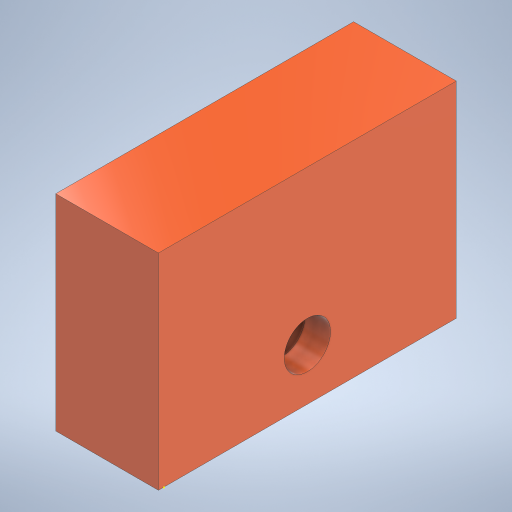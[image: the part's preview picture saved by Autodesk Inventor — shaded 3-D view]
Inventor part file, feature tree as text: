
AUTODESK INVENTOR PART (.ipt)
format: ipt  version: 2024 (Build 280153020, 153B)  size: 206,848 bytes
history: native  units: mm
features: sketch x4, extrude x3
ambient origin geometry x8: Origin, YZ Plane, XZ Plane, XY Plane, X Axis, Y Axis, Z Axis, Center Point
bodies: Solid1 (feature_tree)
feature tree (7):
  extrude  "Extrusion1"  Depth=20.0mm
  sketch  "Sketch6"  dims[d15=2.5mm d16=0.0mm d17=0.5mm]
  extrude  "Extrusion6"  Depth=0.5mm
  extrude  "Extrusion7"  Depth=10.0mm TaperAngle=0.0deg
  sketch  "Sketch1"  dims[d0=20.0mm d1=0.0mm d14=4.5mm]
  sketch  "Sketch7"  dims[d18=0.5mm d19=10.0mm d20=0.0mm]
  sketch  "Sketch8"
